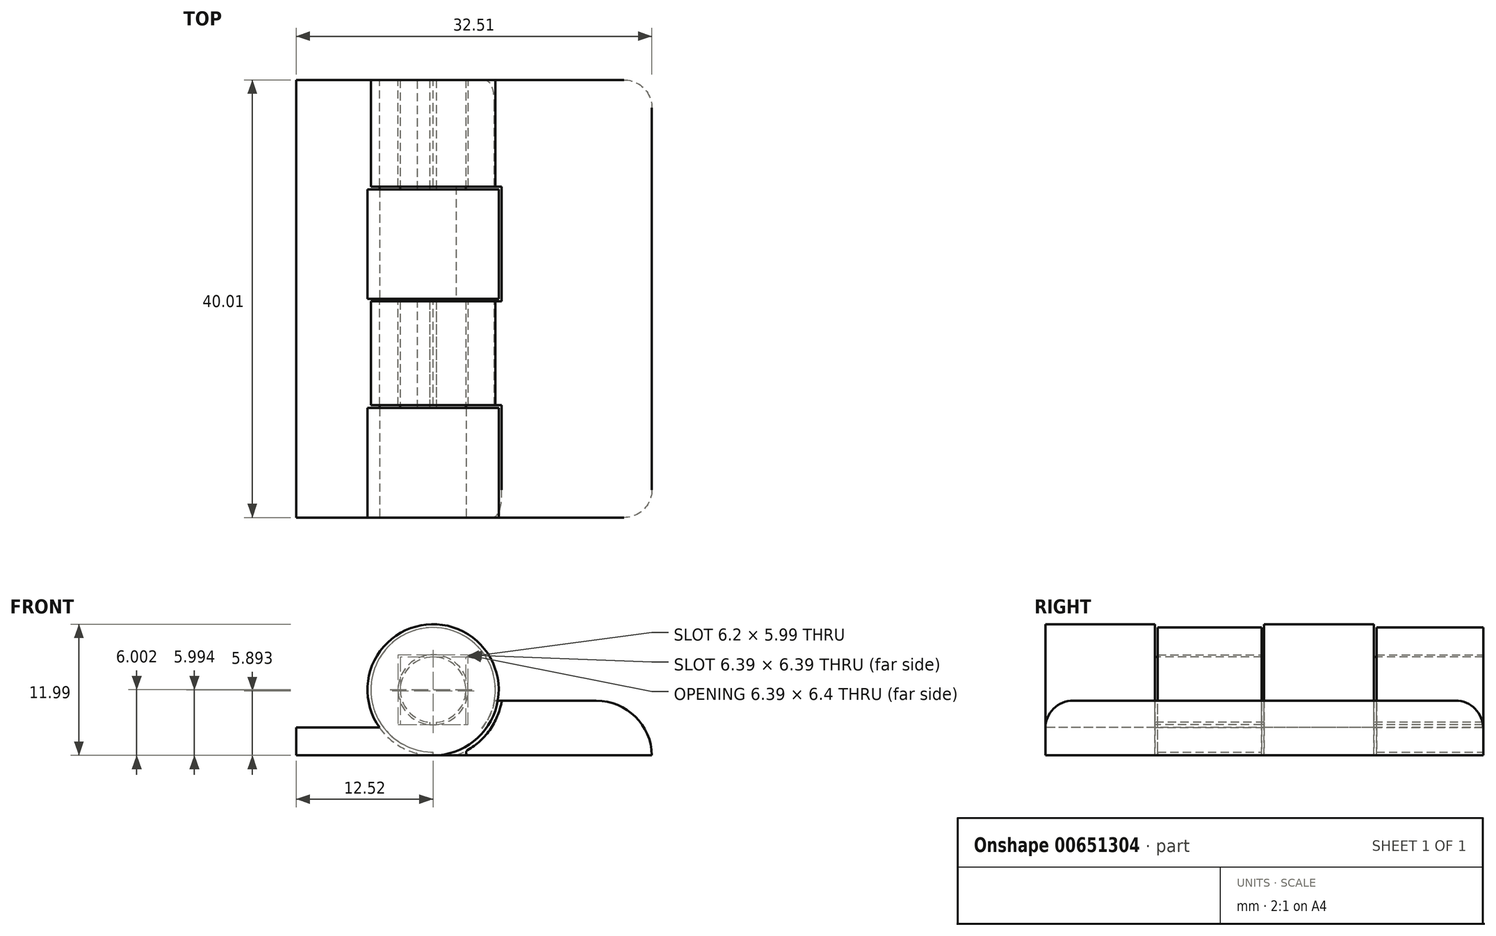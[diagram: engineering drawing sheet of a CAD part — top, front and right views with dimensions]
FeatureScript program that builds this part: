
annotation { "Feature Type Name" : "Feature", "Feature Type Description" : "" }
export const myFeature = defineFeature(function(context is Context, id is Id, definition is map)
    precondition{}
    {
        {
            var Q0;
            Q0=qCreatedBy(makeId("Front.planeOp"),FACE);
            var sketch = newSketch(context, id + "F0", { "sketchPlane" : qUnion([Q0])});
            skLineSegment(sketch, "E0", {"start": v(0, 0) * mm, "end": v(-12.52, 0) * mm});
            skLineSegment(sketch, "E1", {"start": v(-12.52, 0) * mm, "end": v(-12.52, 2.54) * mm});
            skLineSegment(sketch, "E2", {"start": v(-12.52, 2.54) * mm, "end": v(-4.9, 2.54) * mm});
            skCircle(sketch, "E3", {"center": v(0, 6) * mm, "radius": 6 * mm});
            skPoint(sketch, "E4.start.orphan", {"position": v(0, 2.54) * mm});
            skArc(sketch, "E5.0", {"start": v(2.1, 0) * mm, "mid": v(4.87, 1.93) * mm, "end": v(6.27, 5) * mm});
            skLineSegment(sketch, "E6", {"start": v(0, 0) * mm, "end": v(2.1, 0) * mm});
            skLineSegment(sketch, "E7", {"start": v(2.1, 0) * mm, "end": v(19.99, 0) * mm});
            skLineSegment(sketch, "E8", {"start": v(19.99, 0) * mm, "end": v(19.99, 5) * mm});
            skLineSegment(sketch, "E9", {"start": v(19.99, 5) * mm, "end": v(6.27, 5) * mm});
            skLineSegment(sketch, "E10", {"start": v(6.27, 5) * mm, "end": v(5.91, 5) * mm});
            skArc(sketch, "E11", {"start": v(0.3, 3.01) * mm, "mid": v(0, 9) * mm, "end": v(-0.3, 3.01) * mm});
            skLineSegment(sketch, "E12", {"start": v(0.3, 3.01) * mm, "end": v(0.3, 2.8) * mm});
            skLineSegment(sketch, "E13", {"start": v(-0.3, 3.01) * mm, "end": v(-0.3, 2.8) * mm});
            skArc(sketch, "E14", {"start": v(-0.3, 2.8) * mm, "mid": v(0, 2.8) * mm, "end": v(0.3, 2.8) * mm});
            skSolve(sketch);
        }
        {
            var Q0;
            Q0=qCreatedBy(makeId("Front.planeOp"),FACE);
            cPlane(context, id + "F1", {"entities" : qUnion([Q0]), "cplaneType" : CPlaneType.OFFSET, "offset" : 40 * mm, "oppositeDirection" : true, "width" : 152.4 * mm, "height" : 152.4 * mm});
        }
        {
            var Q0;
            Q0=qCreatedBy(id+"F1.planeOp",FACE);
            var sketch = newSketch(context, id + "F2", { "sketchPlane" : qUnion([Q0])});
            skArc(sketch, "E15", {"start": v(-4.9, 2.54) * mm, "mid": v(-3.41, 1.07) * mm, "end": v(-1.51, 0.2) * mm});
            skLineSegment(sketch, "E16", {"start": v(0, 0) * mm, "end": v(19.99, 0) * mm});
            skLineSegment(sketch, "E17", {"start": v(19.99, 0) * mm, "end": v(19.99, 5) * mm});
            skArc(sketch, "E18", {"start": v(5.6, 5) * mm, "mid": v(-3.66, 10.35) * mm, "end": v(0, 0.3) * mm});
            skLineSegment(sketch, "E19", {"start": v(19.99, 5) * mm, "end": v(5.6, 5) * mm});
            skLineSegment(sketch, "E20", {"start": v(-1.54, 0) * mm, "end": v(-12.52, 0) * mm});
            skLineSegment(sketch, "E21", {"start": v(-12.52, 0) * mm, "end": v(-12.52, 2.54) * mm});
            skLineSegment(sketch, "E22", {"start": v(-12.52, 2.54) * mm, "end": v(-4.9, 2.54) * mm});
            skLineSegment(sketch, "E23", {"start": v(0, 0) * mm, "end": v(0, 0.3) * mm});
            skArc(sketch, "E24.trimOffspring", {"start": v(0, 0) * mm, "mid": v(3.87, 1.42) * mm, "end": v(5.91, 5) * mm});
            skArc(sketch, "E25", {"start": v(-1.54, 0) * mm, "mid": v(-1.44, 0.09) * mm, "end": v(-1.51, 0.2) * mm});
            skCircle(sketch, "E26", {"center": v(0, 6) * mm, "radius": 3.2 * mm});
            skSolve(sketch);
        }
        {
            var Q0;
            Q0=makeQuery(id+"F0.imprint","IMPRINT",FACE,{"disambiguationData":[TD([[makeQuery(id+"F0.imprint","IMPRINT",EDGE,{"derivedFrom":sQuery(id+"F0.wireOp",EDGE,"E11")}),-1.0]])]});
            var Q1;
            {var subQ0=sQuery(id+"F0.wireOp",EDGE,"E0");Q1=makeQuery(id+"F0.imprint","IMPRINT",FACE,{"disambiguationData":[TD([[makeQuery(id+"F0.imprint","IMPRINT",EDGE,{"derivedFrom":subQ0}),-1.0]])]});}
            extrude(context, id + "F3", {"entities" : qUnion([Q0, Q1]), "oppositeDirection" : true, "depth" : 10 * mm, "offsetDistance" : 25.4 * mm});
        }
        {
            var Q0;
            Q0=makeQuery(id+"F0.imprint","IMPRINT",FACE,{"disambiguationData":[TD([[makeQuery(id+"F0.imprint","IMPRINT",EDGE,{"derivedFrom":sQuery(id+"F0.wireOp",EDGE,"E11")}),1.0]])]});
            extrude(context, id + "F4", {"entities" : qUnion([Q0]), "operationType" : NewBodyOperationType.ADD, "oppositeDirection" : true, "depth" : 40 * mm, "offsetDistance" : 25.4 * mm});
        }
        {
            var Q0;
            Q0=qCreatedBy(id+"F1.planeOp",FACE);
            cPlane(context, id + "F5", {"entities" : qUnion([Q0]), "cplaneType" : CPlaneType.OFFSET, "offset" : 10 * mm, "width" : 152.4 * mm, "height" : 152.4 * mm});
        }
        {
            var Q0;
            Q0=makeQuery(id+"F0.imprint","IMPRINT",FACE,{"disambiguationData":[TD([[makeQuery(id+"F0.imprint","IMPRINT",EDGE,{"derivedFrom":sQuery(id+"F0.wireOp",EDGE,"E11")}),-1.0]])]});
            var Q1;
            {var subQ0=sQuery(id+"F0.wireOp",EDGE,"E0");Q1=makeQuery(id+"F0.imprint","IMPRINT",FACE,{"disambiguationData":[TD([[makeQuery(id+"F0.imprint","IMPRINT",EDGE,{"derivedFrom":subQ0}),-1.0]])]});}
            var Q2;
            Q2=qCreatedBy(id+"F5.planeOp",FACE);
            extrude(context, id + "F6", {"entities" : qUnion([Q0, Q1]), "operationType" : NewBodyOperationType.ADD, "endBound" : BoundingType.UP_TO_SURFACE, "oppositeDirection" : true, "depth" : 29.46 * mm, "endBoundEntityFace" : qUnion([Q2]), "offsetDistance" : 25.4 * mm, "hasSecondDirection" : true, "secondDirectionOppositeDirection" : true, "secondDirectionDepth" : 19.99 * mm});
        }
        {
            var Q0;
            Q0=makeQuery(id+"F2.imprint","IMPRINT",FACE,{"disambiguationData":[TD([[makeQuery(id+"F2.imprint","IMPRINT",EDGE,{"derivedFrom":sQuery(id+"F2.wireOp",EDGE,"E15")}),-1.0]])]});
            extrude(context, id + "F7", {"entities" : qUnion([Q0]), "operationType" : NewBodyOperationType.ADD, "depth" : 10 * mm, "offsetDistance" : 25.4 * mm});
        }
        {
            var Q0;
            Q0=makeQuery(id+"F3.opExtrude","CAP_FACE",FACE,{"disambiguationData":[OSD([sQuery(id+"F0.wireOp",EDGE,"E0"),sQuery(id+"F0.wireOp",EDGE,"E1"),sQuery(id+"F0.wireOp",EDGE,"E2"),sQuery(id+"F0.wireOp",EDGE,"E3"),sQuery(id+"F0.wireOp",EDGE,"E11"),sQuery(id+"F0.wireOp",EDGE,"E12"),sQuery(id+"F0.wireOp",EDGE,"E13"),sQuery(id+"F0.wireOp",EDGE,"E14")])],"isStart":false});
            cPlane(context, id + "F8", {"entities" : qUnion([Q0]), "cplaneType" : CPlaneType.OFFSET, "offset" : 0.25 * mm, "width" : 152.4 * mm, "height" : 152.4 * mm});
        }
        {
            var Q0;
            {var subQ2=sQuery(id+"F2.wireOp",EDGE,"E18");Q0=makeQuery(id+"F2.imprint","IMPRINT",FACE,{"disambiguationData":[TD([[makeQuery(id+"F2.imprint","IMPRINT",EDGE,{"derivedFrom":subQ2}),1.0]])]});}
            var Q1;
            Q1=makeQuery(id+"F2.imprint","IMPRINT",FACE,{"disambiguationData":[TD([[makeQuery(id+"F2.imprint","IMPRINT",EDGE,{"derivedFrom":sQuery(id+"F2.wireOp",EDGE,"E16")}),1.0]])]});
            var Q2;
            Q2=qCreatedBy(id+"F8.planeOp",FACE);
            extrude(context, id + "F9", {"entities" : qUnion([Q0, Q1]), "operationType" : NewBodyOperationType.ADD, "endBound" : BoundingType.UP_TO_SURFACE, "depth" : 25.4 * mm, "endBoundEntityFace" : qUnion([Q2]), "offsetDistance" : 25.4 * mm, "hasSecondDirection" : true, "secondDirectionOppositeDirection" : false, "secondDirectionDepth" : 20.24 * mm});
        }
        {
            var Q0;
            Q0=makeQuery(id+"F0.imprint","IMPRINT",FACE,{"disambiguationData":[TD([[makeQuery(id+"F0.imprint","IMPRINT",EDGE,{"derivedFrom":sQuery(id+"F0.wireOp",EDGE,"E5.0")}),-1.0]])]});
            extrude(context, id + "F10", {"entities" : qUnion([Q0]), "operationType" : NewBodyOperationType.ADD, "oppositeDirection" : true, "depth" : 10.26 * mm, "offsetDistance" : 25.4 * mm});
        }
        {
            var Q0;
            Q0=makeQuery(id+"F2.imprint","IMPRINT",FACE,{"disambiguationData":[TD([[makeQuery(id+"F2.imprint","IMPRINT",EDGE,{"derivedFrom":sQuery(id+"F2.wireOp",EDGE,"E15")}),-1.0]])]});
            var Q1;
            Q1=makeQuery(id+"F3.opExtrude","CAP_FACE",FACE,{"disambiguationData":[OSD([sQuery(id+"F0.wireOp",EDGE,"E0"),sQuery(id+"F0.wireOp",EDGE,"E1"),sQuery(id+"F0.wireOp",EDGE,"E2"),sQuery(id+"F0.wireOp",EDGE,"E3"),sQuery(id+"F0.wireOp",EDGE,"E11"),sQuery(id+"F0.wireOp",EDGE,"E12"),sQuery(id+"F0.wireOp",EDGE,"E13"),sQuery(id+"F0.wireOp",EDGE,"E14")])],"isStart":false});
            var Q2;
            Q2=makeQuery(id+"F6.opExtrude","CAP_FACE",FACE,{"disambiguationData":[OSD([sQuery(id+"F0.wireOp",EDGE,"E0"),sQuery(id+"F0.wireOp",EDGE,"E1"),sQuery(id+"F0.wireOp",EDGE,"E2"),sQuery(id+"F0.wireOp",EDGE,"E3"),sQuery(id+"F0.wireOp",EDGE,"E11"),sQuery(id+"F0.wireOp",EDGE,"E12"),sQuery(id+"F0.wireOp",EDGE,"E13"),sQuery(id+"F0.wireOp",EDGE,"E14")])],"isStart":true});
            extrude(context, id + "F11", {"entities" : qUnion([Q0]), "operationType" : NewBodyOperationType.ADD, "endBound" : BoundingType.UP_TO_SURFACE, "depth" : 25.4 * mm, "endBoundEntityFace" : qUnion([Q1]), "offsetDistance" : 25.4 * mm, "hasSecondDirection" : true, "secondDirectionBound" : BoundingType.UP_TO_SURFACE, "secondDirectionOppositeDirection" : false, "secondDirectionDepth" : 28.45 * mm, "secondDirectionBoundEntityFace" : qUnion([Q2])});
        }
        {
            var Q0;
            Q0=makeQuery(id+"F0.imprint","IMPRINT",FACE,{"disambiguationData":[TD([[makeQuery(id+"F0.imprint","IMPRINT",EDGE,{"derivedFrom":sQuery(id+"F0.wireOp",EDGE,"E5.0")}),-1.0]])]});
            var Q1;
            Q1=makeQuery(id+"F13.opExtrude","CAP_FACE",FACE,{"disambiguationData":[OSD([sQuery(id+"F2.wireOp",EDGE,"E16"),sQuery(id+"F2.wireOp",EDGE,"E17"),sQuery(id+"F2.wireOp",EDGE,"E18"),sQuery(id+"F2.wireOp",EDGE,"E19"),sQuery(id+"F2.wireOp",EDGE,"E23"),sQuery(id+"F2.wireOp",EDGE,"E26")])],"isStart":false});
            var Q2;
            Q2=makeQuery(id+"F9.opExtrude","CAP_FACE",FACE,{"disambiguationData":[OSD([sQuery(id+"F2.wireOp",EDGE,"E16"),sQuery(id+"F2.wireOp",EDGE,"E17"),sQuery(id+"F2.wireOp",EDGE,"E18"),sQuery(id+"F2.wireOp",EDGE,"E19"),sQuery(id+"F2.wireOp",EDGE,"E23"),sQuery(id+"F2.wireOp",EDGE,"E26")])],"isStart":true});
            extrude(context, id + "F12", {"entities" : qUnion([Q0]), "operationType" : NewBodyOperationType.ADD, "oppositeDirection" : true, "depth" : 31.37 * mm, "endBoundEntityFace" : qUnion([Q1]), "offsetDistance" : 25.4 * mm, "hasSecondDirection" : true, "secondDirectionBound" : BoundingType.UP_TO_SURFACE, "secondDirectionOppositeDirection" : true, "secondDirectionDepth" : 26.92 * mm, "secondDirectionBoundEntityFace" : qUnion([Q2])});
        }
        {
            var Q0;
            Q0=makeQuery(id+"F2.imprint","IMPRINT",FACE,{"disambiguationData":[TD([[makeQuery(id+"F2.imprint","IMPRINT",EDGE,{"derivedFrom":sQuery(id+"F2.wireOp",EDGE,"E16")}),1.0]])]});
            var Q1;
            {var subQ2=sQuery(id+"F2.wireOp",EDGE,"E18");Q1=makeQuery(id+"F2.imprint","IMPRINT",FACE,{"disambiguationData":[TD([[makeQuery(id+"F2.imprint","IMPRINT",EDGE,{"derivedFrom":subQ2}),1.0]])]});}
            extrude(context, id + "F13", {"entities" : qUnion([Q0, Q1]), "operationType" : NewBodyOperationType.ADD, "depth" : 9.75 * mm, "offsetDistance" : 25.4 * mm});
        }
        {
            var Q0;
            Q0=makeQuery(id+"F12.opExtrude","TWEAK_EDGE",EDGE,{"derivedFrom":[makeQuery(id+"F0.imprint","IMPRINT",EDGE,{"derivedFrom":sQuery(id+"F0.wireOp",EDGE,"E5.0")}),makeQuery(id+"F0.imprint","IMPRINT",EDGE,{"derivedFrom":sQuery(id+"F0.wireOp",EDGE,"E7")})]});
            var Q1;
            Q1=makeQuery(id+"F10.opExtrude","SWEPT_EDGE",EDGE,{"disambiguationData":[OSD([sQuery(id+"F0.wireOp",EDGE,"E5.0"),sQuery(id+"F0.wireOp",EDGE,"E6"),sQuery(id+"F0.wireOp",EDGE,"E7")])]});
            fillet(context, id + "F14", {"entities" : qUnion([Q0, Q1]), "radius" : 0.25 * mm, "tangentPropagation" : true, "allowEdgeOverflow" : false});
        }
        {
            var Q0;
            Q0=makeQuery(id+"F13.opExtrude","SWEPT_EDGE",EDGE,{"disambiguationData":[OSD([sQuery(id+"F2.wireOp",EDGE,"E17"),sQuery(id+"F2.wireOp",EDGE,"E19")])]});
            var Q1;
            Q1=makeQuery(id+"F12.boolean.opBoolean","MERGE",EDGE,{"derivedFrom":[makeQuery(id+"F9.opExtrude","SWEPT_EDGE",EDGE,{"disambiguationData":[OSD([sQuery(id+"F2.wireOp",EDGE,"E17"),sQuery(id+"F2.wireOp",EDGE,"E19")])]}),makeQuery(id+"F12.opExtrude","TWEAK_EDGE",EDGE,{"derivedFrom":[makeQuery(id+"F0.imprint","IMPRINT",EDGE,{"derivedFrom":sQuery(id+"F0.wireOp",EDGE,"E8")}),makeQuery(id+"F0.imprint","IMPRINT",EDGE,{"derivedFrom":sQuery(id+"F0.wireOp",EDGE,"E9")})]})]});
            var Q2;
            Q2=makeQuery(id+"F10.opExtrude","SWEPT_EDGE",EDGE,{"disambiguationData":[OSD([sQuery(id+"F0.wireOp",EDGE,"E8"),sQuery(id+"F0.wireOp",EDGE,"E9")])]});
            fillet(context, id + "F15", {"entities" : qUnion([Q0, Q1, Q2]), "radius" : 5.08 * mm, "tangentPropagation" : true, "allowEdgeOverflow" : false});
        }
        {
            var Q0;
            Q0=makeQuery(id+"F13.opExtrude","CAP_EDGE",EDGE,{"disambiguationData":[OSD([sQuery(id+"F2.wireOp",EDGE,"E19")])],"isStart":true});
            var Q1;
            Q1=makeQuery(id+"F10.opExtrude","CAP_EDGE",EDGE,{"disambiguationData":[OSD([sQuery(id+"F0.wireOp",EDGE,"E9")])],"isStart":true});
            fillet(context, id + "F16", {"entities" : qUnion([Q0, Q1]), "radius" : 2.54 * mm, "tangentPropagation" : true, "allowEdgeOverflow" : false});
        }
    });
